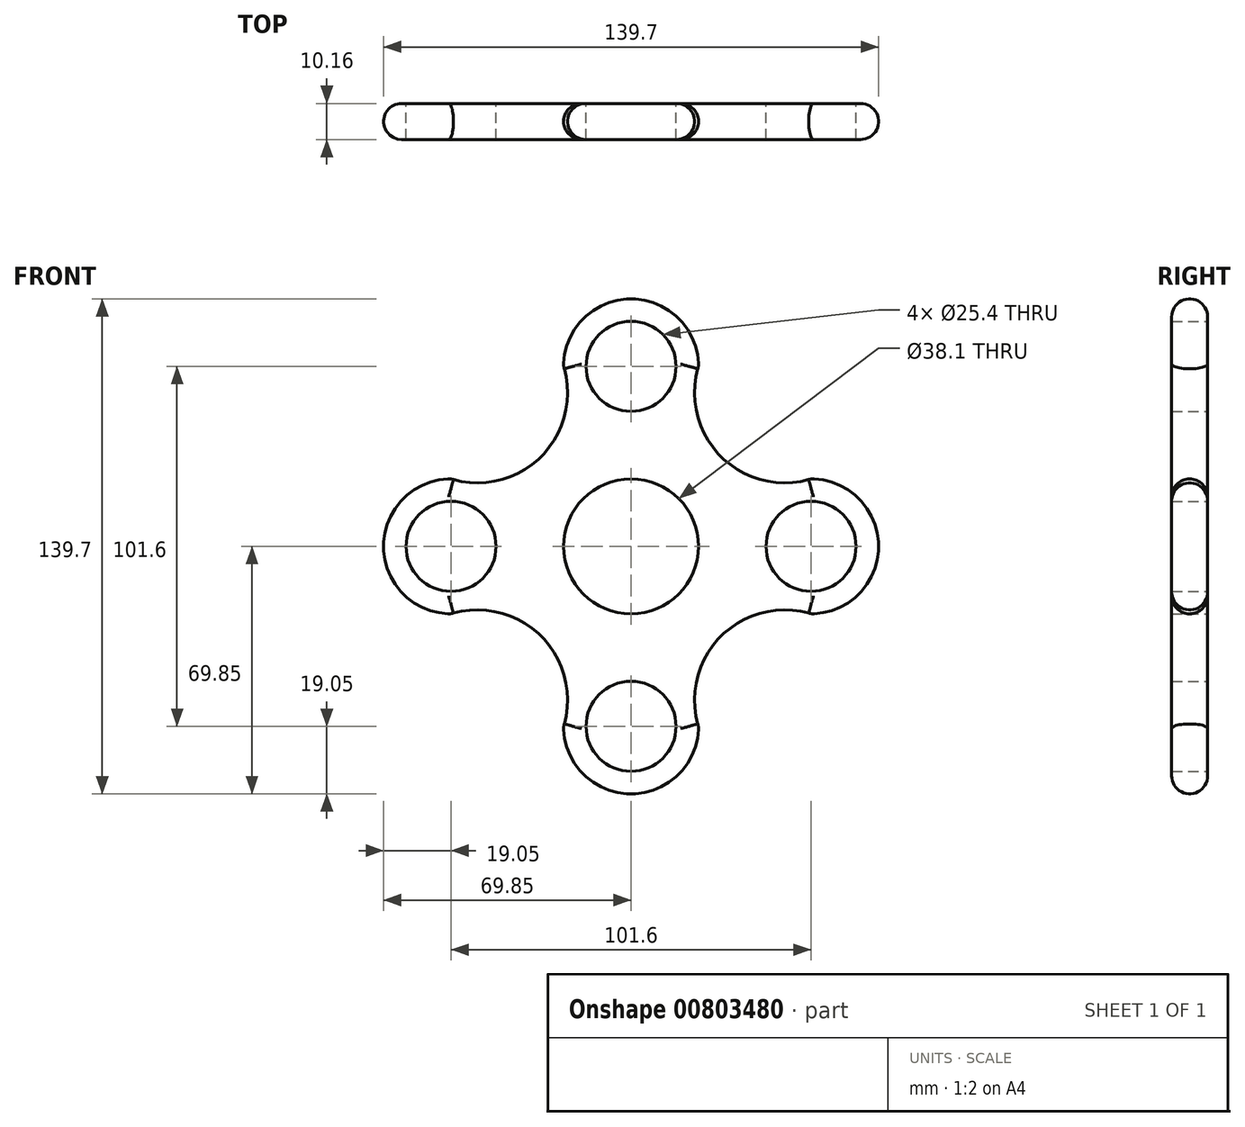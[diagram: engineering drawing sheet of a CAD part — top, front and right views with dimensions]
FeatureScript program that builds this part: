
annotation { "Feature Type Name" : "Feature", "Feature Type Description" : "" }
export const myFeature = defineFeature(function(context is Context, id is Id, definition is map)
    precondition{}
    {
        {
            var Q0;
            Q0=qCreatedBy(makeId("Front.planeOp"),FACE);
            var sketch = newSketch(context, id + "F0", { "sketchPlane" : qUnion([Q0])});
            skCircle(sketch, "E0", {"center": v(0, 0) * mm, "radius": 19.05 * mm});
            skCircle(sketch, "E1", {"center": v(50.8, 0) * mm, "radius": 12.7 * mm});
            skCircle(sketch, "E2", {"center": v(-50.8, 0) * mm, "radius": 12.7 * mm});
            skCircle(sketch, "E3", {"center": v(0, 50.8) * mm, "radius": 12.7 * mm});
            skCircle(sketch, "E4", {"center": v(0, -50.8) * mm, "radius": 12.7 * mm});
            skCircle(sketch, "E5", {"center": v(-50.8, 0) * mm, "radius": 19.05 * mm});
            skCircle(sketch, "E6", {"center": v(0, 50.8) * mm, "radius": 19.05 * mm});
            skCircle(sketch, "E7", {"center": v(50.8, 0) * mm, "radius": 19.05 * mm});
            skCircle(sketch, "E8", {"center": v(0, 0) * mm, "radius": 25.4 * mm});
            skArc(sketch, "E9", {"start": v(-18.71, -47.23) * mm, "mid": v(0, -69.85) * mm, "end": v(18.71, -47.23) * mm});
            skArc(sketch, "E10", {"start": v(18.71, -47.23) * mm, "mid": v(0, -31.75) * mm, "end": v(-18.71, -47.23) * mm});
            skArc(sketch, "E11", {"start": v(-50.8, 19.05) * mm, "mid": v(-25.36, 25.36) * mm, "end": v(-19.05, 50.8) * mm});
            skArc(sketch, "E12", {"start": v(19.05, 50.8) * mm, "mid": v(25.36, 25.36) * mm, "end": v(50.8, 19.05) * mm});
            skArc(sketch, "E13", {"start": v(50.8, -19.05) * mm, "mid": v(25.36, -25.36) * mm, "end": v(19.05, -50.8) * mm});
            skArc(sketch, "E14", {"start": v(-19.05, -50.8) * mm, "mid": v(-25.36, -25.36) * mm, "end": v(-50.8, -19.05) * mm});
            skSolve(sketch);
        }
        {
            var Q0;
            Q0=makeQuery(id+"F0.imprint","IMPRINT",FACE,{"disambiguationData":[TD([[makeQuery(id+"F0.imprint","IMPRINT",EDGE,{"derivedFrom":sQuery(id+"F0.wireOp",EDGE,"E8")}),-1.0]])]});
            var Q1;
            Q1=makeQuery(id+"F0.imprint","IMPRINT",FACE,{"disambiguationData":[TD([[makeQuery(id+"F0.imprint","IMPRINT",EDGE,{"derivedFrom":sQuery(id+"F0.wireOp",EDGE,"E0")}),-1.0]])]});
            var Q2;
            Q2=makeQuery(id+"F0.imprint","IMPRINT",FACE,{"disambiguationData":[TD([[makeQuery(id+"F0.imprint","IMPRINT",EDGE,{"derivedFrom":sQuery(id+"F0.wireOp",EDGE,"E1")}),-1.0]])]});
            var Q3;
            Q3=makeQuery(id+"F0.imprint","IMPRINT",FACE,{"disambiguationData":[TD([[makeQuery(id+"F0.imprint","IMPRINT",EDGE,{"derivedFrom":sQuery(id+"F0.wireOp",EDGE,"E4")}),-1.0]])]});
            var Q4;
            Q4=makeQuery(id+"F0.imprint","IMPRINT",FACE,{"disambiguationData":[TD([[makeQuery(id+"F0.imprint","IMPRINT",EDGE,{"derivedFrom":sQuery(id+"F0.wireOp",EDGE,"E2")}),-1.0]])]});
            var Q5;
            Q5=makeQuery(id+"F0.imprint","IMPRINT",FACE,{"disambiguationData":[TD([[makeQuery(id+"F0.imprint","IMPRINT",EDGE,{"derivedFrom":sQuery(id+"F0.wireOp",EDGE,"E3")}),-1.0]])]});
            extrude(context, id + "F1", {"entities" : qUnion([Q0, Q1, Q2, Q3, Q4, Q5]), "depth" : 10.16 * mm, "offsetDistance" : 25.4 * mm});
        }
        {
            var Q0;
            Q0=makeQuery(id+"F1.opExtrude","CAP_EDGE",EDGE,{"disambiguationData":[OSD([sQuery(id+"F0.wireOp",EDGE,"E14")])],"isStart":true});
            var Q1;
            Q1=makeQuery(id+"F1.opExtrude","CAP_EDGE",EDGE,{"disambiguationData":[OSD([sQuery(id+"F0.wireOp",EDGE,"E14")])],"isStart":false});
            var Q2;
            Q2=makeQuery(id+"F1.opExtrude","CAP_EDGE",EDGE,{"disambiguationData":[OSD([sQuery(id+"F0.wireOp",EDGE,"E13")])],"isStart":true});
            var Q3;
            Q3=makeQuery(id+"F1.opExtrude","CAP_EDGE",EDGE,{"disambiguationData":[OSD([sQuery(id+"F0.wireOp",EDGE,"E13")])],"isStart":false});
            var Q4;
            Q4=makeQuery(id+"F1.opExtrude","CAP_EDGE",EDGE,{"disambiguationData":[OSD([sQuery(id+"F0.wireOp",EDGE,"E11")])],"isStart":false});
            var Q5;
            Q5=makeQuery(id+"F1.opExtrude","CAP_EDGE",EDGE,{"disambiguationData":[OSD([sQuery(id+"F0.wireOp",EDGE,"E11")])],"isStart":true});
            var Q6;
            Q6=makeQuery(id+"F1.opExtrude","CAP_EDGE",EDGE,{"disambiguationData":[OSD([sQuery(id+"F0.wireOp",EDGE,"E12")])],"isStart":false});
            var Q7;
            Q7=makeQuery(id+"F1.opExtrude","CAP_EDGE",EDGE,{"disambiguationData":[OSD([sQuery(id+"F0.wireOp",EDGE,"E12")])],"isStart":true});
            fillet(context, id + "F2", {"entities" : qUnion([Q0, Q1, Q2, Q3, Q4, Q5, Q6, Q7]), "radius" : 5.08 * mm, "tangentPropagation" : true, "allowEdgeOverflow" : false});
        }
        {
            var Q0;
            Q0=makeQuery(id+"F1.opExtrude","CAP_EDGE",EDGE,{"disambiguationData":[OSD([sQuery(id+"F0.wireOp",EDGE,"E9")])],"isStart":false});
            var Q1;
            Q1=makeQuery(id+"F1.opExtrude","CAP_EDGE",EDGE,{"disambiguationData":[OSD([sQuery(id+"F0.wireOp",EDGE,"E9")])],"isStart":true});
            var Q2;
            Q2=makeQuery(id+"F2.opFillet","BLEND_EDGE",EDGE,{"blendedFrom":[makeQuery(id+"F1.opExtrude","CAP_EDGE",EDGE,{"disambiguationData":[OSD([sQuery(id+"F0.wireOp",EDGE,"E14")])],"isStart":false}),makeQuery(id+"F1.opExtrude","SWEPT_FACE",FACE,{"disambiguationData":[OSD([sQuery(id+"F0.wireOp",EDGE,"E9")])]})],"blendedInto":[makeQuery(id+"F1.opExtrude","SWEPT_FACE",FACE,{"disambiguationData":[OSD([sQuery(id+"F0.wireOp",EDGE,"E9")])]})]});
            var Q3;
            Q3=makeQuery(id+"F2.opFillet","BLEND_EDGE",EDGE,{"blendedFrom":[makeQuery(id+"F1.opExtrude","CAP_EDGE",EDGE,{"disambiguationData":[OSD([sQuery(id+"F0.wireOp",EDGE,"E14")])],"isStart":true}),makeQuery(id+"F1.opExtrude","SWEPT_FACE",FACE,{"disambiguationData":[OSD([sQuery(id+"F0.wireOp",EDGE,"E9")])]})],"blendedInto":[makeQuery(id+"F1.opExtrude","SWEPT_FACE",FACE,{"disambiguationData":[OSD([sQuery(id+"F0.wireOp",EDGE,"E9")])]})]});
            var Q4;
            Q4=makeQuery(id+"F2.opFillet","BLEND_EDGE",EDGE,{"blendedFrom":[makeQuery(id+"F1.opExtrude","CAP_EDGE",EDGE,{"disambiguationData":[OSD([sQuery(id+"F0.wireOp",EDGE,"E13")])],"isStart":false}),makeQuery(id+"F1.opExtrude","SWEPT_FACE",FACE,{"disambiguationData":[OSD([sQuery(id+"F0.wireOp",EDGE,"E9")])]})],"blendedInto":[makeQuery(id+"F1.opExtrude","SWEPT_FACE",FACE,{"disambiguationData":[OSD([sQuery(id+"F0.wireOp",EDGE,"E9")])]})]});
            var Q5;
            Q5=makeQuery(id+"F2.opFillet","BLEND_EDGE",EDGE,{"blendedFrom":[makeQuery(id+"F1.opExtrude","CAP_EDGE",EDGE,{"disambiguationData":[OSD([sQuery(id+"F0.wireOp",EDGE,"E13")])],"isStart":true}),makeQuery(id+"F1.opExtrude","SWEPT_FACE",FACE,{"disambiguationData":[OSD([sQuery(id+"F0.wireOp",EDGE,"E9")])]})],"blendedInto":[makeQuery(id+"F1.opExtrude","SWEPT_FACE",FACE,{"disambiguationData":[OSD([sQuery(id+"F0.wireOp",EDGE,"E9")])]})]});
            fillet(context, id + "F3", {"entities" : qUnion([Q0, Q1, Q2, Q3, Q4, Q5]), "radius" : 5.08 * mm, "tangentPropagation" : true, "allowEdgeOverflow" : false});
        }
        {
            var Q0;
            Q0=makeQuery(id+"F1.opExtrude","CAP_EDGE",EDGE,{"disambiguationData":[OSD([sQuery(id+"F0.wireOp",EDGE,"E6")])],"isStart":false});
            var Q1;
            Q1=makeQuery(id+"F2.opFillet","BLEND_EDGE",EDGE,{"blendedFrom":[makeQuery(id+"F1.opExtrude","CAP_EDGE",EDGE,{"disambiguationData":[OSD([sQuery(id+"F0.wireOp",EDGE,"E12")])],"isStart":false}),makeQuery(id+"F1.opExtrude","SWEPT_FACE",FACE,{"disambiguationData":[OSD([sQuery(id+"F0.wireOp",EDGE,"E6")])]})],"blendedInto":[makeQuery(id+"F1.opExtrude","SWEPT_FACE",FACE,{"disambiguationData":[OSD([sQuery(id+"F0.wireOp",EDGE,"E6")])]})]});
            var Q2;
            Q2=makeQuery(id+"F2.opFillet","BLEND_EDGE",EDGE,{"blendedFrom":[makeQuery(id+"F1.opExtrude","CAP_EDGE",EDGE,{"disambiguationData":[OSD([sQuery(id+"F0.wireOp",EDGE,"E12")])],"isStart":true}),makeQuery(id+"F1.opExtrude","SWEPT_FACE",FACE,{"disambiguationData":[OSD([sQuery(id+"F0.wireOp",EDGE,"E6")])]})],"blendedInto":[makeQuery(id+"F1.opExtrude","SWEPT_FACE",FACE,{"disambiguationData":[OSD([sQuery(id+"F0.wireOp",EDGE,"E6")])]})]});
            var Q3;
            Q3=makeQuery(id+"F1.opExtrude","CAP_EDGE",EDGE,{"disambiguationData":[OSD([sQuery(id+"F0.wireOp",EDGE,"E6")])],"isStart":true});
            var Q4;
            Q4=makeQuery(id+"F2.opFillet","BLEND_EDGE",EDGE,{"blendedFrom":[makeQuery(id+"F1.opExtrude","CAP_EDGE",EDGE,{"disambiguationData":[OSD([sQuery(id+"F0.wireOp",EDGE,"E11")])],"isStart":false}),makeQuery(id+"F1.opExtrude","SWEPT_FACE",FACE,{"disambiguationData":[OSD([sQuery(id+"F0.wireOp",EDGE,"E6")])]})],"blendedInto":[makeQuery(id+"F1.opExtrude","SWEPT_FACE",FACE,{"disambiguationData":[OSD([sQuery(id+"F0.wireOp",EDGE,"E6")])]})]});
            var Q5;
            Q5=makeQuery(id+"F2.opFillet","BLEND_EDGE",EDGE,{"blendedFrom":[makeQuery(id+"F1.opExtrude","CAP_EDGE",EDGE,{"disambiguationData":[OSD([sQuery(id+"F0.wireOp",EDGE,"E11")])],"isStart":true}),makeQuery(id+"F1.opExtrude","SWEPT_FACE",FACE,{"disambiguationData":[OSD([sQuery(id+"F0.wireOp",EDGE,"E6")])]})],"blendedInto":[makeQuery(id+"F1.opExtrude","SWEPT_FACE",FACE,{"disambiguationData":[OSD([sQuery(id+"F0.wireOp",EDGE,"E6")])]})]});
            fillet(context, id + "F4", {"entities" : qUnion([Q0, Q1, Q2, Q3, Q4, Q5]), "radius" : 5.08 * mm, "tangentPropagation" : true, "allowEdgeOverflow" : false});
        }
        {
            var Q0;
            Q0=makeQuery(id+"F2.opFillet","BLEND_EDGE",EDGE,{"blendedFrom":[makeQuery(id+"F1.opExtrude","CAP_EDGE",EDGE,{"disambiguationData":[OSD([sQuery(id+"F0.wireOp",EDGE,"E11")])],"isStart":false}),makeQuery(id+"F1.opExtrude","SWEPT_FACE",FACE,{"disambiguationData":[OSD([sQuery(id+"F0.wireOp",EDGE,"E5")])]})],"blendedInto":[makeQuery(id+"F1.opExtrude","SWEPT_FACE",FACE,{"disambiguationData":[OSD([sQuery(id+"F0.wireOp",EDGE,"E5")])]})]});
            var Q1;
            Q1=makeQuery(id+"F2.opFillet","BLEND_EDGE",EDGE,{"blendedFrom":[makeQuery(id+"F1.opExtrude","CAP_EDGE",EDGE,{"disambiguationData":[OSD([sQuery(id+"F0.wireOp",EDGE,"E13")])],"isStart":true}),makeQuery(id+"F1.opExtrude","SWEPT_FACE",FACE,{"disambiguationData":[OSD([sQuery(id+"F0.wireOp",EDGE,"E7")])]})],"blendedInto":[makeQuery(id+"F1.opExtrude","SWEPT_FACE",FACE,{"disambiguationData":[OSD([sQuery(id+"F0.wireOp",EDGE,"E7")])]})]});
            fillet(context, id + "F5", {"entities" : qUnion([Q0, Q1]), "radius" : 5.08 * mm, "tangentPropagation" : true, "allowEdgeOverflow" : false});
        }
    });
